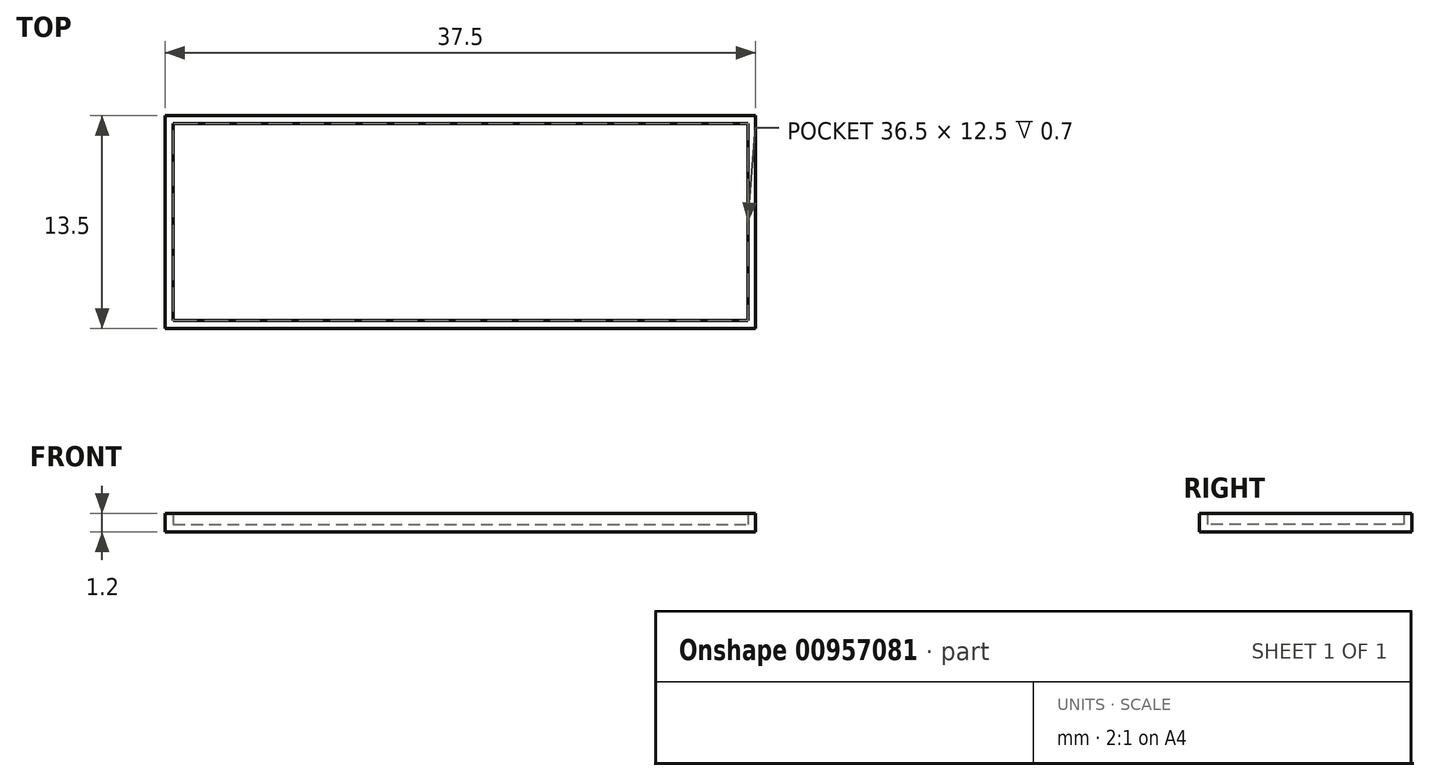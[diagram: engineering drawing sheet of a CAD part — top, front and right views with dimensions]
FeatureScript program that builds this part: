
annotation { "Feature Type Name" : "Feature", "Feature Type Description" : "" }
export const myFeature = defineFeature(function(context is Context, id is Id, definition is map)
    precondition{}
    {
        {
            var Q0;
            Q0=qCreatedBy(makeId("Top.planeOp"),FACE);
            var sketch = newSketch(context, id + "F0", { "sketchPlane" : qUnion([Q0])});
            skLineSegment(sketch, "E0.bottom", {"start": v(-36.3, -11.04) * mm, "end": v(1.2, -11.04) * mm});
            skLineSegment(sketch, "E0.top", {"start": v(-36.3, -24.54) * mm, "end": v(1.2, -24.54) * mm});
            skLineSegment(sketch, "E0.left", {"start": v(-36.3, -11.04) * mm, "end": v(-36.3, -24.54) * mm});
            skLineSegment(sketch, "E0.right", {"start": v(1.2, -11.04) * mm, "end": v(1.2, -24.54) * mm});
            skSolve(sketch);
        }
        {
            var Q0;
            Q0 = qSketchRegion(id + "F0", true);
            extrude(context, id + "F1", {"entities" : qUnion([Q0]), "depth" : 1.2 * mm, "offsetDistance" : 25 * mm});
        }
        {
            var Q0;
            Q0=makeQuery(id+"F1.opExtrude","CAP_FACE",FACE,{"disambiguationData":[OSD([sQuery(id+"F0.wireOp",EDGE,"E0.bottom"),sQuery(id+"F0.wireOp",EDGE,"E0.top"),sQuery(id+"F0.wireOp",EDGE,"E0.left"),sQuery(id+"F0.wireOp",EDGE,"E0.right")])],"isStart":false});
            shell(context, id + "F2", {"entities" : qUnion([Q0]), "thickness" : .5 * mm});
        }
    });
